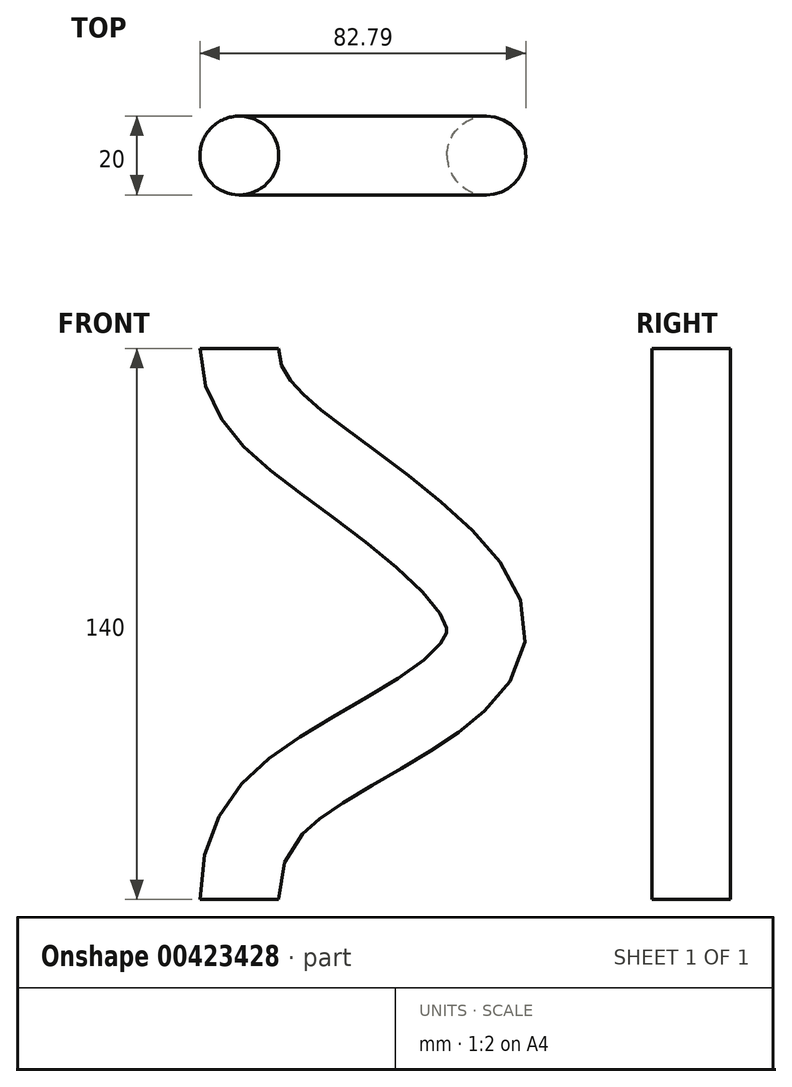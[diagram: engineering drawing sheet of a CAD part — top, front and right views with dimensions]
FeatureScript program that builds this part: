
annotation { "Feature Type Name" : "Feature", "Feature Type Description" : "" }
export const myFeature = defineFeature(function(context is Context, id is Id, definition is map)
    precondition{}
    {
        {
            var Q0;
            Q0=qCreatedBy(makeId("Front.planeOp"),FACE);
            var sketch = newSketch(context, id + "F0", { "sketchPlane" : qUnion([Q0])});
            skFitSpline(sketch, "E0", {"points": [v(0, 140) * mm, v(22.06, 110.75) * mm, v(62.78, 67.75) * mm, v(24.83, 35.35) * mm, v(0, 0) * mm], "startDerivative": vector(0, -164.1) * mm, "endDerivative": vector(-0.05, -229.39) * mm});
            skSolve(sketch);
        }
        {
            var Q0;
            Q0=sQuery(id+"F0.wireOp",VERTEX,"E0.start");
            var Q1;
            Q1=sQuery(id+"F0.wireOp",EDGE,"E0");
            cPlane(context, id + "F1", {"entities" : qUnion([Q0, Q1]), "cplaneType" : CPlaneType.CURVE_POINT, "offset" : 25 * mm, "width" : 150 * mm, "height" : 150 * mm});
        }
        {
            var Q0;
            Q0=qCreatedBy(id+"F1.planeOp",FACE);
            var sketch = newSketch(context, id + "F2", { "sketchPlane" : qUnion([Q0])});
            skCircle(sketch, "E1", {"center": v(0, 0) * mm, "radius": 10 * mm});
            skSolve(sketch);
        }
        {
            var Q0;
            Q0=makeQuery(id+"F2.imprint","IMPRINT",FACE,{"disambiguationData":[TD([[makeQuery(id+"F2.imprint","IMPRINT",EDGE,{"derivedFrom":sQuery(id+"F2.wireOp",EDGE,"E1")}),1.0]])]});
            var Q1;
            Q1=sQuery(id+"F0.wireOp",EDGE,"E0");
            sweep(context, id + "F3", {"profiles" : qUnion([Q0]), "path" : qUnion([Q1])});
        }
    });
